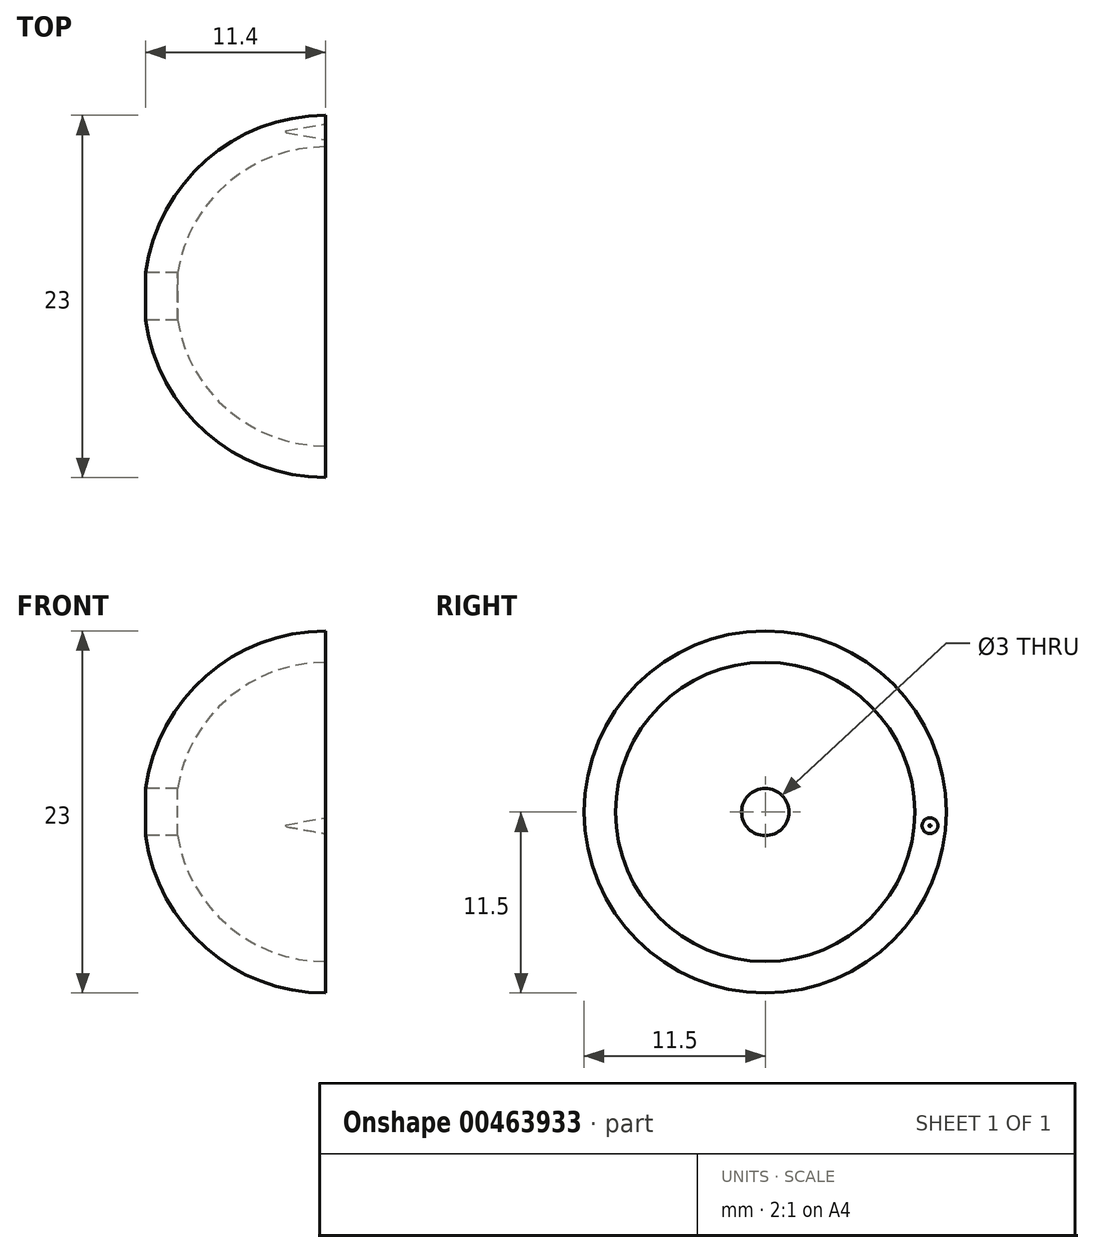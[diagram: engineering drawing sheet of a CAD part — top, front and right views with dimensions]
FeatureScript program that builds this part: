
annotation { "Feature Type Name" : "Feature", "Feature Type Description" : "" }
export const myFeature = defineFeature(function(context is Context, id is Id, definition is map)
    precondition{}
    {
        {
            var Q0;
            Q0=qCreatedBy(makeId("Top.planeOp"),FACE);
            var sketch = newSketch(context, id + "F0", { "sketchPlane" : qUnion([Q0])});
            skArc(sketch, "E0", {"start": v(0, -11.5) * mm, "mid": v(11.5, 0) * mm, "end": v(0, 11.5) * mm});
            skLineSegment(sketch, "E1", {"start": v(0, 11.5) * mm, "end": v(0, -11.5) * mm});
            skSolve(sketch);
        }
        {
            var Q0;
            Q0=makeQuery(id+"F0.imprint","IMPRINT",FACE,{"disambiguationData":[TD([[makeQuery(id+"F0.imprint","IMPRINT",EDGE,{"derivedFrom":sQuery(id+"F0.wireOp",EDGE,"E0")}),1.0]])]});
            var Q1;
            Q1=sQuery(id+"F0.wireOp",EDGE,"E1");
            revolve(context, id + "F1", {"entities" : qUnion([Q0]), "axis" : qUnion([Q1]), "revolveType" : RevolveType.FULL});
        }
        {
            var Q0;
            Q0=qCreatedBy(makeId("Top.planeOp"),FACE);
            var sketch = newSketch(context, id + "F2", { "sketchPlane" : qUnion([Q0])});
            skLineSegment(sketch, "E2.bottom", {"start": v(0, 20.33) * mm, "end": v(26.75, 20.33) * mm});
            skLineSegment(sketch, "E2.top", {"start": v(0, -20.54) * mm, "end": v(26.75, -20.54) * mm});
            skLineSegment(sketch, "E2.left", {"start": v(0, 20.33) * mm, "end": v(0, -20.54) * mm});
            skLineSegment(sketch, "E2.right", {"start": v(26.75, 20.33) * mm, "end": v(26.75, -20.54) * mm});
            skSolve(sketch);
        }
        {
            var Q0;
            Q0 = qSketchRegion(id + "F2", true);
            extrude(context, id + "F3", {"entities" : qUnion([Q0]), "operationType" : NewBodyOperationType.REMOVE, "oppositeDirection" : true, "depth" : 25 * mm, "hasSecondDirection" : true, "secondDirectionOppositeDirection" : false, "secondDirectionDepth" : 37.9 * mm});
        }
        {
            var Q0;
            Q0=qCreatedBy(makeId("Right.planeOp"),FACE);
            cPlane(context, id + "F4", {"entities" : qUnion([Q0]), "cplaneType" : CPlaneType.OFFSET, "offset" : 11.5 * mm, "oppositeDirection" : true, "width" : 150 * mm, "height" : 150 * mm});
        }
        {
            var Q0;
            Q0=qCreatedBy(id+"F4.planeOp",FACE);
            var sketch = newSketch(context, id + "F5", { "sketchPlane" : qUnion([Q0])});
            skCircle(sketch, "E3", {"center": v(0, 0) * mm, "radius": 1.5 * mm});
            skSolve(sketch);
        }
        {
            var Q0;
            Q0 = qSketchRegion(id + "F5", true);
            extrude(context, id + "F6", {"entities" : qUnion([Q0]), "operationType" : NewBodyOperationType.REMOVE, "depth" : 25 * mm});
        }
        {
            var Q0;
            Q0=makeQuery(id+"F3.boolean.opBoolean","COPY",FACE,{"derivedFrom":makeQuery(id+"F3.opExtrude","SWEPT_FACE",FACE,{"disambiguationData":[OSD([sQuery(id+"F2.wireOp",EDGE,"E2.left")])]})});
            var sketch = newSketch(context, id + "F7", { "sketchPlane" : qUnion([Q0])});
            skArc(sketch, "E4", {"start": v(0, -9.5) * mm, "mid": v(9.5, 0) * mm, "end": v(0, 9.5) * mm});
            skLineSegment(sketch, "E5", {"start": v(0, 9.5) * mm, "end": v(0, -9.5) * mm});
            skSolve(sketch);
        }
        {
            var Q0;
            Q0 = qSketchRegion(id + "F7", true);
            var Q1;
            Q1=sQuery(id+"F7.wireOp",EDGE,"E5");
            revolve(context, id + "F8", {"operationType" : NewBodyOperationType.REMOVE, "entities" : qUnion([Q0]), "axis" : qUnion([Q1]), "revolveType" : RevolveType.FULL, "oppositeDirection" : true});
        }
        {
            var Q0;
            Q0=makeQuery(id+"F3.boolean.opBoolean","COPY",FACE,{"derivedFrom":makeQuery(id+"F3.opExtrude","SWEPT_FACE",FACE,{"disambiguationData":[OSD([sQuery(id+"F2.wireOp",EDGE,"E2.left")])]})});
            var sketch = newSketch(context, id + "F9", { "sketchPlane" : qUnion([Q0])});
            skCircle(sketch, "E6", {"center": v(10.46, -0.87) * mm, "radius": 0.5 * mm});
            skSolve(sketch);
        }
        {
            var Q0;
            Q0=makeQuery(id+"F9.imprint","IMPRINT",FACE,{"disambiguationData":[TD([[makeQuery(id+"F9.imprint","IMPRINT",EDGE,{"derivedFrom":sQuery(id+"F9.wireOp",EDGE,"E6")}),1.0]])]});
            extrude(context, id + "F10", {"entities" : qUnion([Q0]), "operationType" : NewBodyOperationType.REMOVE, "oppositeDirection" : true, "depth" : 2.5 * mm, "hasDraft" : true, "draftAngle" : 10 * degree, "draftPullDirection" : true});
        }
    });
